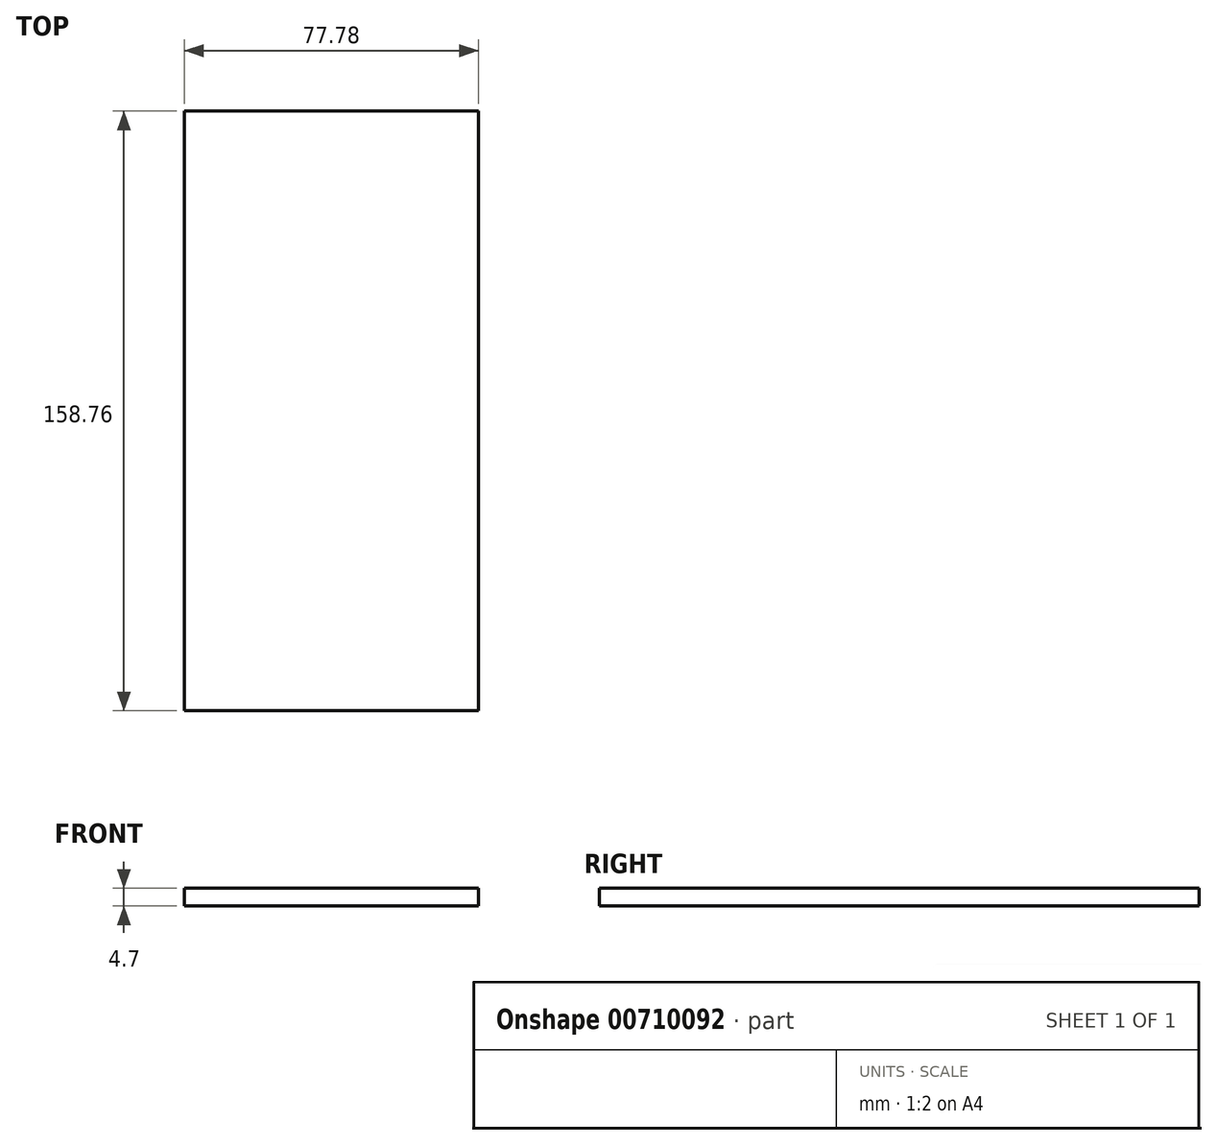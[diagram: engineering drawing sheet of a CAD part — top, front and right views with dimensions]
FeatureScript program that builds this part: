
annotation { "Feature Type Name" : "Feature", "Feature Type Description" : "" }
export const myFeature = defineFeature(function(context is Context, id is Id, definition is map)
    precondition{}
    {
        {
            var Q0;
            Q0=qCreatedBy(makeId("Top.planeOp"),FACE);
            var sketch = newSketch(context, id + "F0", { "sketchPlane" : qUnion([Q0])});
            skLineSegment(sketch, "E0.bottom", {"start": v(38.89, -79.37) * mm, "end": v(-38.89, -79.37) * mm});
            skLineSegment(sketch, "E0.top", {"start": v(38.89, 79.38) * mm, "end": v(-38.89, 79.38) * mm});
            skLineSegment(sketch, "E0.left", {"start": v(38.89, -79.37) * mm, "end": v(38.89, 79.38) * mm});
            skLineSegment(sketch, "E0.right", {"start": v(-38.89, -79.37) * mm, "end": v(-38.89, 79.38) * mm});
            skPoint(sketch, "E0.middle", {"position": v(0, 0) * mm});
            skSolve(sketch);
        }
        {
            var Q0;
            Q0=makeQuery(id+"F0.imprint","IMPRINT",FACE,{"disambiguationData":[TD([[makeQuery(id+"F0.imprint","IMPRINT",EDGE,{"derivedFrom":sQuery(id+"F0.wireOp",EDGE,"E0.bottom")}),-1.0]])]});
            extrude(context, id + "F1", {"entities" : qUnion([Q0]), "depth" : 4.7 * mm, "offsetDistance" : 25.4 * mm});
        }
    });
